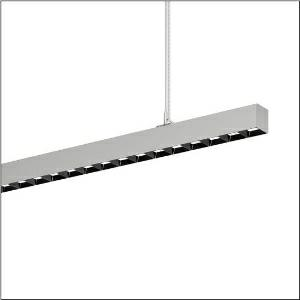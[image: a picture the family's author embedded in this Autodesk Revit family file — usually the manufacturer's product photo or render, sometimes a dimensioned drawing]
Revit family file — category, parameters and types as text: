
# Revit family: silica_21_51mx31dc4dsb
name_source: partatom
category: Lighting Fixtures
units: mm (PartAtom-declared; Revit-internal decimal feet)

## family parameters
Cut with Voids When Loaded = No
Host = Face
Light Source = No
Part Type = Normal
Room Calculation Point = No
Round Connector Dimension = Use Diameter
Shared = No

## types (1)
- --- (1 x LED, 18230 lm, 105.9 W, 4000K)
    Apparent Load = 106 VA
    CIE Flux Codes = 87 99 100 59 100
    Color Rendering = 80
    Color Temperature = 4000K
    Default Elevation = 1800 mm
    Description = Silica 21, office luminaire, primary light control with darklight reflector, of PMMA, black, CAT 2 (L<= 3000cd/m²), light emission: direct/indirect distribution, primary light characteristic: symmetric, installation type: suspended mounting, LED, rated luminous flux: 18.230lm, luminous efficacy: 172lm/W, light colour: 840, colour temperature: 4000K, control gear: DALI 2, with terminal, 3+2-pole, max. 2.5mm², mains connection: 220..240V, AC, 50/60Hz, rated input power: 105.9W, luminaire housing, of aluminium, metallic grey (RAL 9006), length: 3.004mm, width: 53mm, height: 53mm, protection rating (complete): IP20, insulation class (complete): insulation class I (protective earthing), certification: CE, permissible operating ambient temperature: 0..+35°C, standard: EN 50419, packaging unit: 1 piece
    Height = 53 mm
    Lamp = 1 x LED
    Lamp Light Flux = 18230 lm
    Lamp Power = 105.9 W
    Lamp count = 1
    Length = 3004 mm
    Luminous efficacy = 172 lm/W
    Manufacturer = Siteco
    ModVariant = No
    Model = 51MX31DC4DSB
    Mounting Place = Ceiling
    Mounting Type = Pendant
    Number of Poles = 1
    OnlyDefault = Yes
    Power Factor = 1
    Product Name = Silica 21
    Product group = office luminaire | ceiling pendant
    ProductGroupID = 903
    Protection Class = Protection class I
    Protection Degree = IP 20
    RLX_Detail_Level = 1
    RLX_Emergency_Light_Flux = 0 lm
    RLX_Emergency_Type = 0
    RLX_Emergency_Type_DB = No
    RlxData = <blob elided: 64921 chars, md5=1c8eddf3>
    Socket = socket
    Standby Power = 0 W
    System Light Flux = 18230 lm
    System Power = 106 W
    Type Comments = factory setting: luminous flux: 100 % | dim-lin: 254 | 367 mA
    Type Image = l_1335859.jpg
    URL = http://relux.com
    VarID = @adj_121143
    Voltage = 0 V
    Weight = 0.00 kg
    Width = 53 mm

## geometry (parser evidence)
native form markers: Blend x4, Sweep x12
no freeform markers — native parametric forms only
